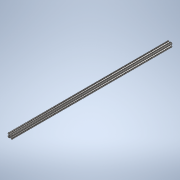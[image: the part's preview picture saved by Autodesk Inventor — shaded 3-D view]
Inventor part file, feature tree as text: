
AUTODESK INVENTOR PART (.ipt)
format: ipt  version: 2020 (Build 240168000, 168)  size: 247,296 bytes
history: native  units: in
note: dims shown in document units (in); Inventor stores cm internally (conversion verified against a paired STEP export)
features: extrude x1, sketch x1
ambient origin geometry x8: Origin, YZ Plane, XZ Plane, XY Plane, X Axis, Y Axis, Z Axis, Center Point
bodies: Solid1 (feature_tree)
feature tree (2):
  extrude  "Extrusion1"  [1 undecoded]
  sketch  "Sketch1"  dims[d0=38.0in d1=0.0in]
note: 1 required parameter value undecoded (feature->parameter linkage not recoverable at this tier; creation-order binding heuristic only, values carry confidence <= 0.55)
